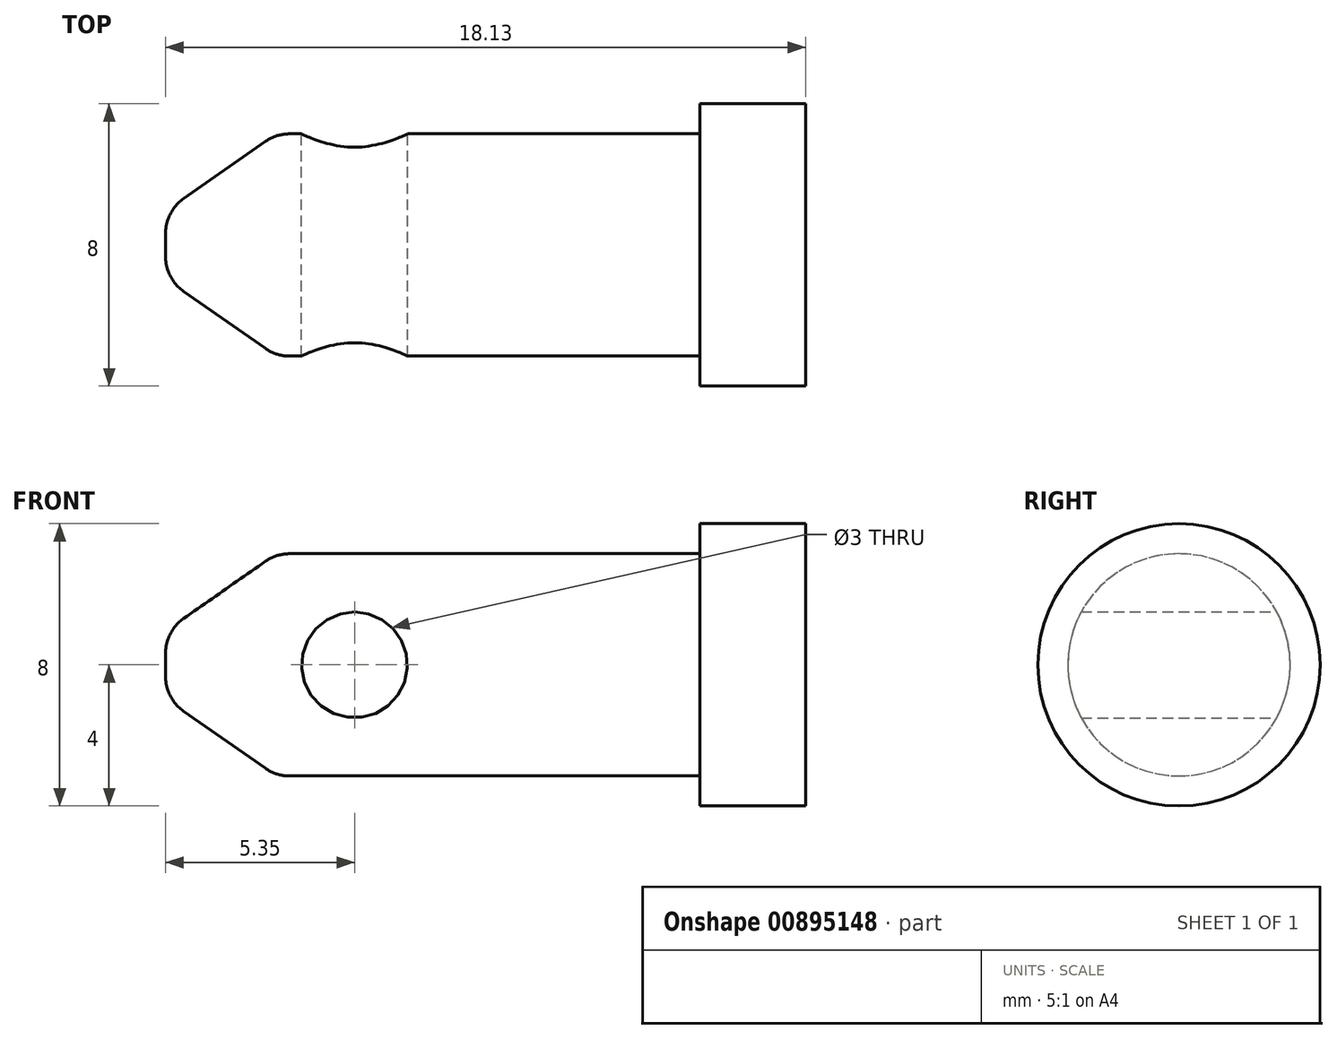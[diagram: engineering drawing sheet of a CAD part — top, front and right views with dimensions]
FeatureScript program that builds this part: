
annotation { "Feature Type Name" : "Feature", "Feature Type Description" : "" }
export const myFeature = defineFeature(function(context is Context, id is Id, definition is map)
    precondition{}
    {
        {
            var Q0;
            Q0=qCreatedBy(makeId("Front.planeOp"),FACE);
            var sketch = newSketch(context, id + "F0", { "sketchPlane" : qUnion([Q0])});
            skLineSegment(sketch, "E0", {"start": v(-26.73, 0) * mm, "end": v(31.98, 0) * mm, "construction": true});
            skLineSegment(sketch, "E1", {"start": v(-7.72, 3.15) * mm, "end": v(4.28, 3.15) * mm});
            skLineSegment(sketch, "E2", {"start": v(4.28, 3.15) * mm, "end": v(4.28, 4) * mm});
            skLineSegment(sketch, "E3", {"start": v(4.28, 4) * mm, "end": v(7.28, 4) * mm});
            skLineSegment(sketch, "E4", {"start": v(7.28, 4) * mm, "end": v(7.28, 0) * mm});
            skLineSegment(sketch, "E5", {"start": v(-10.85, 0) * mm, "end": v(7.28, 0) * mm});
            skLineSegment(sketch, "E6", {"start": v(-10.85, 0) * mm, "end": v(-10.85, 0.95) * mm});
            skLineSegment(sketch, "E7", {"start": v(-10.85, 0.95) * mm, "end": v(-7.72, 3.15) * mm});
            skSolve(sketch);
        }
        {
            var Q0;
            Q0=makeQuery(id+"F0.imprint","IMPRINT",FACE,{"disambiguationData":[TD([[makeQuery(id+"F0.imprint","IMPRINT",EDGE,{"derivedFrom":sQuery(id+"F0.wireOp",EDGE,"E1")}),-1.0]])]});
            var Q1;
            Q1=sQuery(id+"F0.wireOp",EDGE,"E0");
            revolve(context, id + "F1", {"surfaceOperationType" : NewSurfaceOperationType.NEW, "entities" : qUnion([Q0]), "axis" : qUnion([Q1]), "revolveType" : RevolveType.FULL});
        }
        {
            var Q0;
            Q0=makeQuery(id+"F1.opRevolve","SWEPT_EDGE",EDGE,{"disambiguationData":[OSD([sQuery(id+"F0.wireOp",EDGE,"E6"),sQuery(id+"F0.wireOp",EDGE,"E7")])]});
            var Q1;
            Q1=makeQuery(id+"F1.opRevolve","SWEPT_EDGE",EDGE,{"disambiguationData":[OSD([sQuery(id+"F0.wireOp",EDGE,"E1"),sQuery(id+"F0.wireOp",EDGE,"E7")])]});
            fillet(context, id + "F2", {"entities" : qUnion([Q0, Q1]), "tangentPropagation" : true, "radius" : 1.2 * mm, "defaultsChanged" : false, "vertexSettings" : [], "allowEdgeOverflow" : false});
        }
        {
            var Q0;
            Q0=qCreatedBy(makeId("Front.planeOp"),FACE);
            var sketch = newSketch(context, id + "F3", { "sketchPlane" : qUnion([Q0])});
            skCircle(sketch, "E8", {"center": v(-5.5, 0) * mm, "radius": 1.5 * mm});
            skSolve(sketch);
        }
        {
            var Q0;
            Q0 = qSketchRegion(id + "F3", true);
            extrude(context, id + "F4", {"entities" : qUnion([Q0]), "operationType" : NewBodyOperationType.REMOVE, "endBound" : BoundingType.THROUGH_ALL, "depth" : 25 * mm, "offsetDistance" : 25 * mm});
        }
        {
            var Q0;
            Q0=qCreatedBy(makeId("Front.planeOp"),FACE);
            var sketch = newSketch(context, id + "F5", { "sketchPlane" : qUnion([Q0])});
            skCircle(sketch, "E9", {"center": v(-5.5, 0) * mm, "radius": 1.5 * mm});
            skSolve(sketch);
        }
        {
            var Q0;
            Q0 = qSketchRegion(id + "F5", true);
            extrude(context, id + "F6", {"entities" : qUnion([Q0]), "operationType" : NewBodyOperationType.REMOVE, "endBound" : BoundingType.THROUGH_ALL, "oppositeDirection" : true, "depth" : 25 * mm, "offsetDistance" : 25 * mm});
        }
    });
